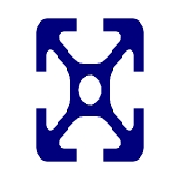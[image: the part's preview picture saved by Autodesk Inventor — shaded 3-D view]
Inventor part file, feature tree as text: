
AUTODESK INVENTOR PART (.ipt)
format: ipt  version: 2020 (Build 240168000, 168)  size: 274,944 bytes
history: native  units: mm
features: other x16, sketch x8
ambient origin geometry x8: Origin, YZ Plane, XZ Plane, XY Plane, X Axis, Y Axis, Z Axis, Center Point
bodies: Body (feature_tree)
feature tree (24):
  other  "Řízená délka"
  other  "Těleso1"
  other  "Start Plane"
  other  "End Plane"
  other  "iFeatureSketch"
  other  "DRAZKA_20:1"
  other  "DRAZKA_20:2"
  other  "DRAZKA_20:3"
  other  "DRAZKA_20:4"
  other  "DIRA_20:1"
  other  "DRAZKA_20:1Axis"
  other  "DRAZKA_20:2Axis"
  other  "DRAZKA_20:3Axis"
  other  "DRAZKA_20:4Axis"
  other  "DIRA_20:1Axis"
  sketch  "Sketch"  dims[d2=20.0mm d3=20.0mm d4=2.0mm d9=-0.0mm d10=267.0mm d11=0.13mm d12=0.0mm d15=0.83mm d16=0.83mm d17=9.8mm d18=3.0mm d19=4.55mm d20=45.0deg d21=5.2mm d22=1.8mm d24=1.0mm d26=0.83mm d27=0.83mm d28=9.8mm d29=3.0mm d30=4.55mm d31=45.0deg d32=5.2mm d33=1.8mm d35=1.0mm d37=0.83mm d38=0.83mm d39=9.8mm d40=3.0mm d41=4.55mm d42=45.0deg d43=5.2mm d44=1.8mm d46=1.0mm d48=0.83mm d49=0.83mm d50=9.8mm d51=3.0mm d52=4.55mm d53=45.0deg d54=5.2mm d55=1.8mm d57=1.0mm d59=4.3mm d60=0.0mm d61=0.0mm d62=0.0mm d63=0.0mm d64=0.0mm d65=0.0mm d66=0.0mm d67=0.0mm d76=90.0deg d14=267.0mm]
  sketch  "Náčrt11"
  other  "Pracovní rovina4"
  sketch  "Náčrt12"
  sketch  "Náčrt6"
  sketch  "Náčrt7"
  sketch  "Náčrt8"
  sketch  "Náčrt9"
  sketch  "Náčrt10"
